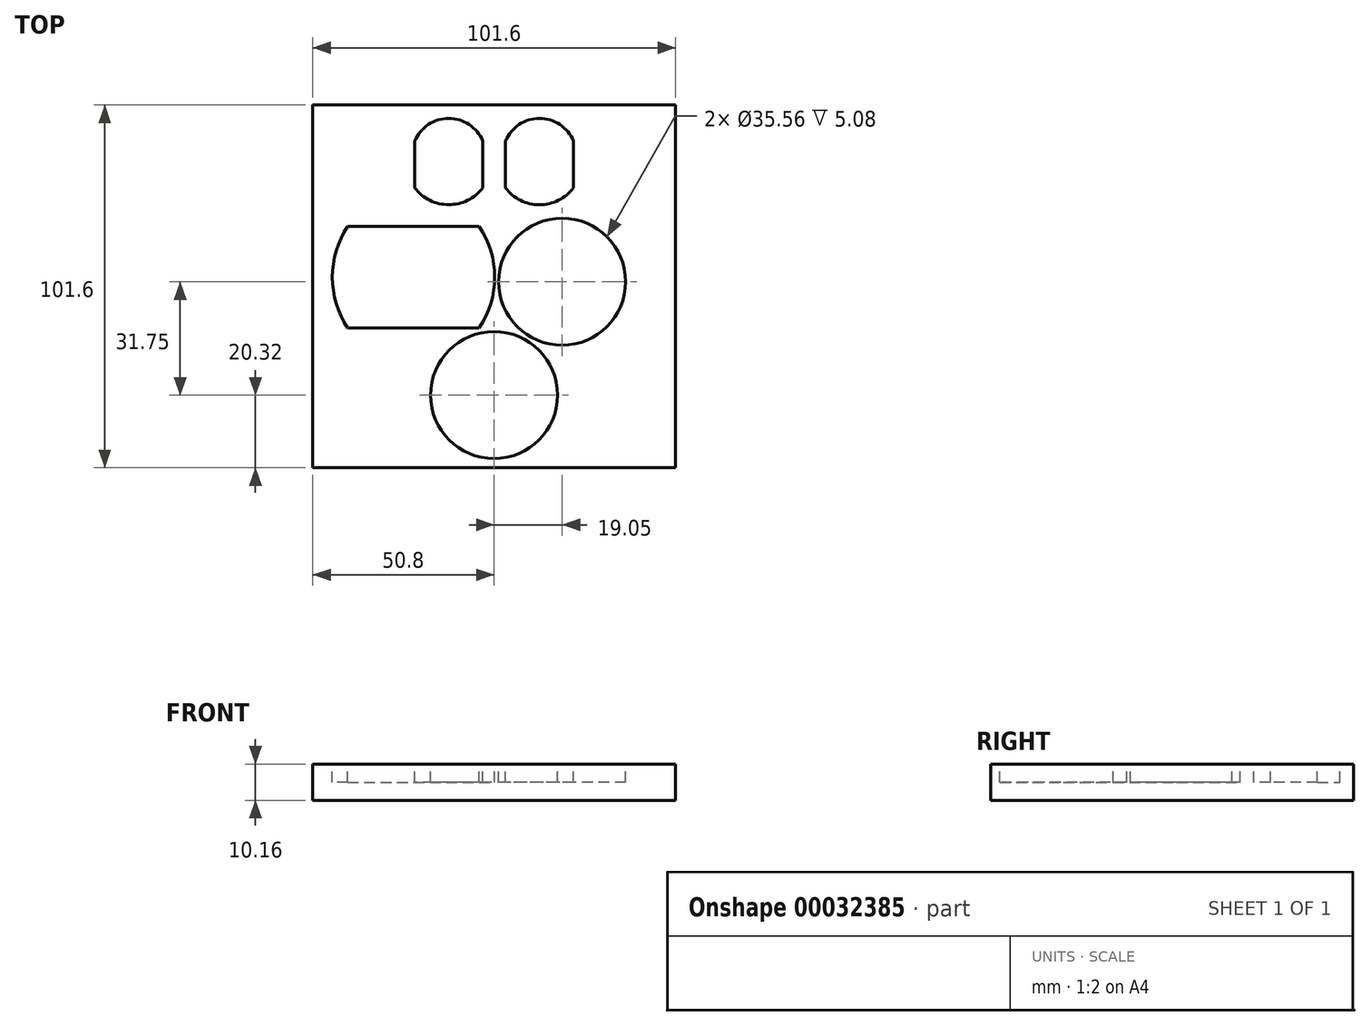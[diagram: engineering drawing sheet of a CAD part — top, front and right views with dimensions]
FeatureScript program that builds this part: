
annotation { "Feature Type Name" : "Feature", "Feature Type Description" : "" }
export const myFeature = defineFeature(function(context is Context, id is Id, definition is map)
    precondition{}
    {
        {
            var Q0;
            Q0=qCreatedBy(makeId("Top.planeOp"),FACE);
            var sketch = newSketch(context, id + "F0", { "sketchPlane" : qUnion([Q0])});
            skLineSegment(sketch, "E0.bottom", {"start": v(-50.8, 50.8) * mm, "end": v(50.8, 50.8) * mm});
            skLineSegment(sketch, "E0.top", {"start": v(-50.8, -50.8) * mm, "end": v(50.8, -50.8) * mm});
            skLineSegment(sketch, "E0.left", {"start": v(-50.8, 50.8) * mm, "end": v(-50.8, -50.8) * mm});
            skLineSegment(sketch, "E0.right", {"start": v(50.8, 50.8) * mm, "end": v(50.8, -50.8) * mm});
            skSolve(sketch);
        }
        {
            var Q0;
            Q0 = qSketchRegion(id + "F0", true);
            extrude(context, id + "F1", {"entities" : qUnion([Q0]), "depth" : 10.16 * mm});
        }
        {
            var Q0;
            Q0=makeQuery(id+"F1.opExtrude","CAP_FACE",FACE,{"disambiguationData":[OSD([sQuery(id+"F0.wireOp",EDGE,"E0.bottom"),sQuery(id+"F0.wireOp",EDGE,"E0.top"),sQuery(id+"F0.wireOp",EDGE,"E0.left"),sQuery(id+"F0.wireOp",EDGE,"E0.right")])],"isStart":false});
            var sketch = newSketch(context, id + "F2", { "sketchPlane" : qUnion([Q0])});
            skCircle(sketch, "E1", {"center": v(0, -30.48) * mm, "radius": 17.78 * mm});
            skCircle(sketch, "E2", {"center": v(19.05, 1.27) * mm, "radius": 17.78 * mm});
            skArc(sketch, "E3", {"start": v(-40.98, 16.76) * mm, "mid": v(-45.3, 2.54) * mm, "end": v(-40.98, -11.68) * mm});
            skArc(sketch, "E4", {"start": v(-4.15, -11.68) * mm, "mid": v(0.17, 2.54) * mm, "end": v(-4.15, 16.76) * mm});
            skLineSegment(sketch, "E5", {"start": v(-40.98, 16.76) * mm, "end": v(-4.15, 16.76) * mm});
            skLineSegment(sketch, "E6", {"start": v(-4.15, -11.68) * mm, "end": v(-40.98, -11.68) * mm});
            skArc(sketch, "E7", {"start": v(3.17, 27.58) * mm, "mid": v(12.7, 22.85) * mm, "end": v(22.23, 27.58) * mm});
            skArc(sketch, "E8", {"start": v(-22.23, 27.58) * mm, "mid": v(-12.7, 22.86) * mm, "end": v(-3.18, 27.58) * mm});
            skArc(sketch, "E9", {"start": v(22.22, 40.71) * mm, "mid": v(12.7, 47.02) * mm, "end": v(3.17, 40.71) * mm});
            skArc(sketch, "E10", {"start": v(-3.18, 40.71) * mm, "mid": v(-12.7, 47) * mm, "end": v(-22.23, 40.71) * mm});
            skLineSegment(sketch, "E11", {"start": v(-22.23, 40.71) * mm, "end": v(-22.23, 27.58) * mm});
            skLineSegment(sketch, "E12", {"start": v(-3.18, 27.58) * mm, "end": v(-3.18, 40.71) * mm});
            skLineSegment(sketch, "E13", {"start": v(3.17, 40.71) * mm, "end": v(3.17, 27.58) * mm});
            skLineSegment(sketch, "E14", {"start": v(22.23, 27.58) * mm, "end": v(22.22, 40.71) * mm});
            skSolve(sketch);
        }
        {
            var Q0;
            Q0 = qSketchRegion(id + "F2", true);
            extrude(context, id + "F3", {"entities" : qUnion([Q0]), "operationType" : NewBodyOperationType.REMOVE, "oppositeDirection" : true, "depth" : 5.08 * mm});
        }
    });
